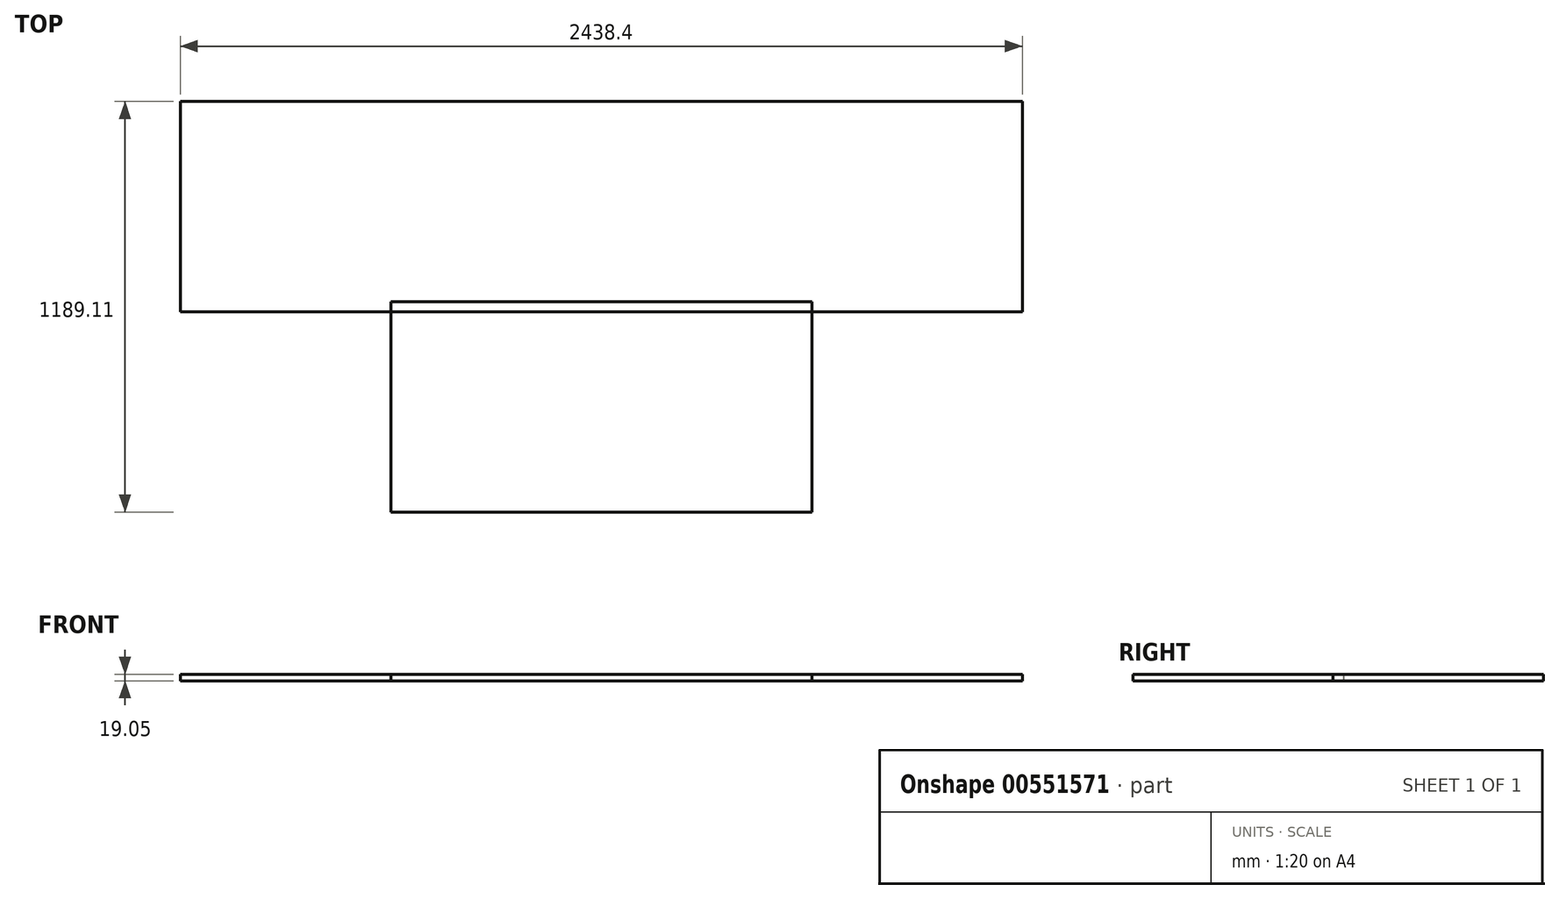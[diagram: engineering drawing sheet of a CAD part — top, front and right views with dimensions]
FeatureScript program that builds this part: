
annotation { "Feature Type Name" : "Feature", "Feature Type Description" : "" }
export const myFeature = defineFeature(function(context is Context, id is Id, definition is map)
    precondition{}
    {
        {
            var Q0;
            Q0=qCreatedBy(makeId("Top.planeOp"),FACE);
            var sketch = newSketch(context, id + "F0", { "sketchPlane" : qUnion([Q0])});
            skLineSegment(sketch, "E0.bottom", {"start": v(1219.2, 343.4) * mm, "end": v(-1219.2, 343.4) * mm});
            skLineSegment(sketch, "E0.top", {"start": v(1219.2, -266.2) * mm, "end": v(-1219.2, -266.2) * mm});
            skLineSegment(sketch, "E0.left", {"start": v(1219.2, 343.4) * mm, "end": v(1219.2, -266.2) * mm});
            skLineSegment(sketch, "E0.right", {"start": v(-1219.2, 343.4) * mm, "end": v(-1219.2, -266.2) * mm});
            skPoint(sketch, "E0.middle", {"position": v(0, 38.6) * mm});
            skSolve(sketch);
        }
        {
            var Q0;
            Q0=makeQuery(id+"F0.imprint","IMPRINT",FACE,{"disambiguationData":[TD([[makeQuery(id+"F0.imprint","IMPRINT",EDGE,{"derivedFrom":sQuery(id+"F0.wireOp",EDGE,"E0.bottom")}),1.0]])]});
            extrude(context, id + "F1", {"entities" : qUnion([Q0]), "depth" : 19.05 * mm, "offsetDistance" : 25.4 * mm});
        }
        {
            var Q0;
            Q0=qCreatedBy(makeId("Top.planeOp"),FACE);
            var sketch = newSketch(context, id + "F2", { "sketchPlane" : qUnion([Q0])});
            skLineSegment(sketch, "E1.bottom", {"start": v(609.6, -236.1) * mm, "end": v(-609.6, -236.1) * mm});
            skLineSegment(sketch, "E1.top", {"start": v(609.6, -845.7) * mm, "end": v(-609.6, -845.7) * mm});
            skLineSegment(sketch, "E1.left", {"start": v(609.6, -236.1) * mm, "end": v(609.6, -845.7) * mm});
            skLineSegment(sketch, "E1.right", {"start": v(-609.6, -236.1) * mm, "end": v(-609.6, -845.7) * mm});
            skPoint(sketch, "E1.middle", {"position": v(0, -540.9) * mm});
            skSolve(sketch);
        }
        {
            var Q0;
            Q0=makeQuery(id+"F2.imprint","IMPRINT",FACE,{"disambiguationData":[TD([[makeQuery(id+"F2.imprint","IMPRINT",EDGE,{"derivedFrom":sQuery(id+"F2.wireOp",EDGE,"E1.bottom")}),1.0]])]});
            extrude(context, id + "F3", {"entities" : qUnion([Q0]), "depth" : 19.05 * mm, "offsetDistance" : 25.4 * mm});
        }
    });
